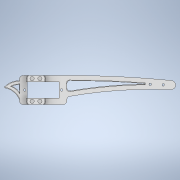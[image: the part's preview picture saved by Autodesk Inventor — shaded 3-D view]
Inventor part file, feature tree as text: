
AUTODESK INVENTOR PART (.ipt)
format: ipt  version: 2020.3 (Build 243373000, 373)  size: 333,312 bytes
history: native  units: mm
features: fillet x7, hole x3, sketch x2, extrude x2, chamfer x1
ambient origin geometry x8: Origin, YZ Plane, XZ Plane, XY Plane, X Axis, Y Axis, Z Axis, Center Point
bodies: Solid1 (feature_tree)
feature tree (15):
  sketch  "Sketch1"  dims[d4=6.0mm d5=24.6mm d6=12.4mm d7=5.0mm d15=7.0mm]
  extrude  "Extrusion1"  Depth=24.6mm
  fillet  "Fillet1"  Radius=12.4mm
  fillet  "Fillet2"  Radius=5.0mm
  fillet  "Fillet3"  Radius=7.0mm
  hole  "Hole1"  [1 undecoded]
  fillet  "Fillet4"  Radius=20.0mm
  hole  "Hole2"  [1 undecoded]
  extrude  "Extrusion3"  Depth=0.5mm
  sketch  "Sketch3"  dims[d17=6.0mm d18=4.0mm d21=20.0mm d23=80.0mm d24=15.0mm d29=29.670597mm d30=6.0mm d31=10.0mm d33=6.0mm d34=0.0mm d40=3.0mm d41=3.0mm d42=2.0mm d43=4.0mm d44=3.0mm d45=4.0mm d50=13.0mm d51=12.0mm d52=22.68928mm d53=16.057029mm d54=2.0mm d55=50.8mm d56=4.0mm d57=2.0mm d58=90.0deg d59=8.0mm d60=20.594885mm d61=0.5mm d62=2.0mm d63=4.0mm d64=4.0mm d65=2.0mm d66=90.0deg d67=8.0mm d68=20.594885mm d69=20.92mm d70=0.0mm d71=2.0mm d80=2.0mm d81=2.0mm d82=45.0deg d87=0.5mm d88=0.5mm d89=6.8mm d90=28.4mm d91=6.0mm d99=3.3mm d100=6.0mm d101=4.0mm d102=2.0mm d103=90.0deg d104=4.3mm d105=0.0mm]
  hole  "Hole5"  [1 undecoded]
  fillet  "Fillet5"  Radius=6.0mm
  chamfer  "Chamfer2"  Distance=10.0mm
  fillet  "Fillet8"  Radius=6.0mm
  fillet  "Fillet9"  Radius=3.0mm
note: 3 required parameter values undecoded (feature->parameter linkage not recoverable at this tier; creation-order binding heuristic only, values carry confidence <= 0.55)
